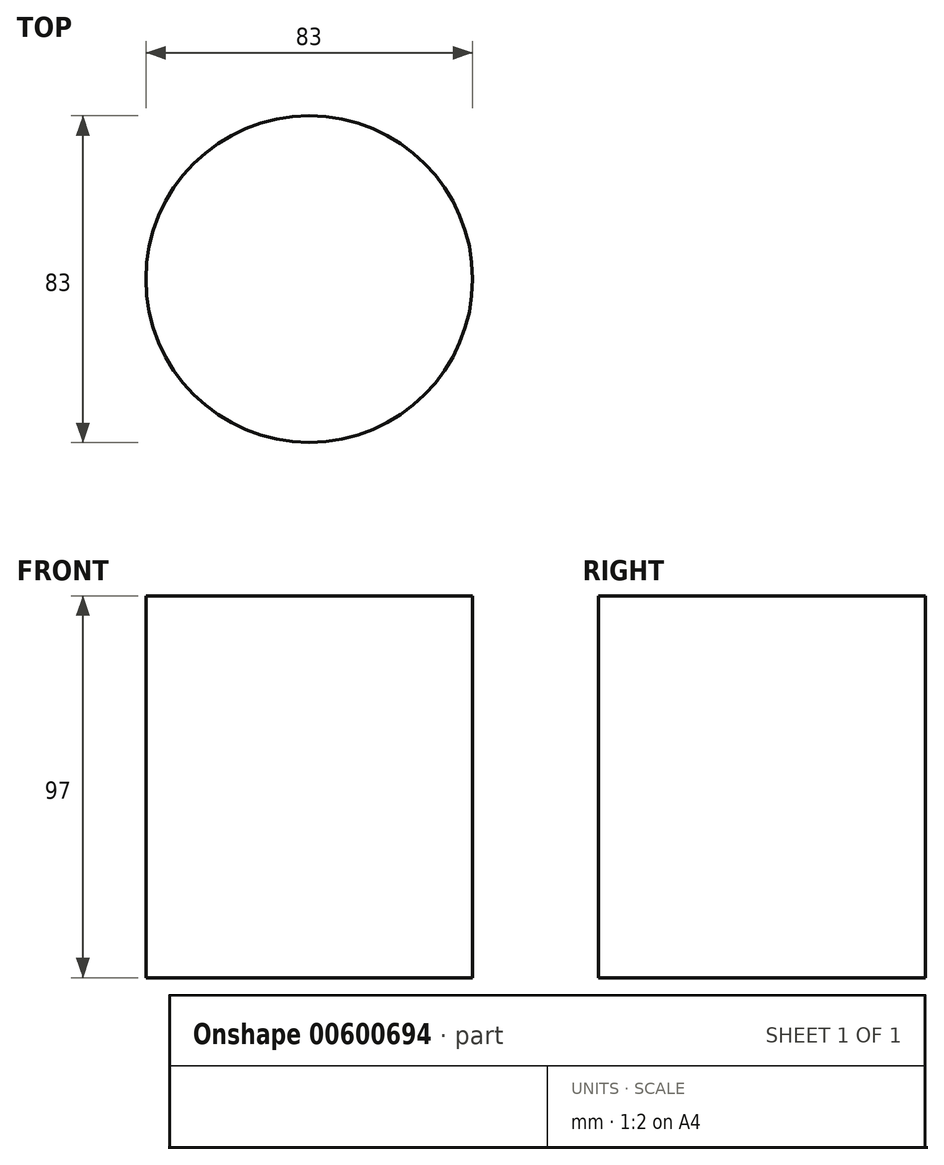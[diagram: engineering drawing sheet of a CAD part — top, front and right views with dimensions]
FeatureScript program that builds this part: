
annotation { "Feature Type Name" : "Feature", "Feature Type Description" : "" }
export const myFeature = defineFeature(function(context is Context, id is Id, definition is map)
    precondition{}
    {
        {
            var Q0;
            Q0=qCreatedBy(makeId("Top.planeOp"),FACE);
            var sketch = newSketch(context, id + "F0", { "sketchPlane" : qUnion([Q0])});
            skCircle(sketch, "E0", {"center": v(0, 0) * mm, "radius": 41.5 * mm});
            skSolve(sketch);
        }
        {
            var Q0;
            Q0=makeQuery(id+"F0.imprint","IMPRINT",FACE,{"disambiguationData":[TD([[makeQuery(id+"F0.imprint","IMPRINT",EDGE,{"derivedFrom":sQuery(id+"F0.wireOp",EDGE,"E0")}),1.0]])]});
            extrude(context, id + "F1", {"entities" : qUnion([Q0]), "depth" : 97 * mm, "offsetDistance" : 25 * mm});
        }
    });
